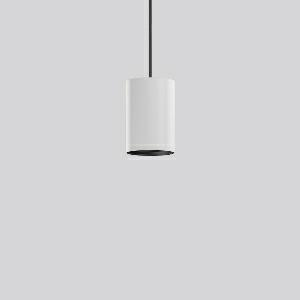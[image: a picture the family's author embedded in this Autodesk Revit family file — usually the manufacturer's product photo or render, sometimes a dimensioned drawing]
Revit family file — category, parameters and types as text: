
# Revit family: deecos_p_maxi_911538_002_3_a3c1
name_source: partatom
category: Lighting Fixtures
units: mm (PartAtom-declared; Revit-internal decimal feet)

## family parameters
Cut with Voids When Loaded = No
Host = Face
Light Source = No
Part Type = Normal
Room Calculation Point = No
Round Connector Dimension = Use Diameter
Shared = No

## types (1)
- DEECOS P maxi (1 x LED Modul 935, 4400 lm, 3500)
    Apparent Load = 35 VA
    Approval mark = CE
    CIE Flux Codes = 100 100 100 100 100
    Color Rendering = 92
    Color Temperature = 3500
    Default Elevation = 1800 mm
    Description = Series: DEECOS P maxi
Cylindrical pendant luminaire. Housing: die-cast aluminium, powder-coated. Canopy made of powder-coated sheet steel with magnetic attachment. Optical assembly with reflector made of MIRO-Silver with 98% total light reflection for outstanding efficiency - can be changed without tools. Best colour rendering index Ra>90. Transparent suspension cable 2 m, can be shortened. High quality converter without flickering and stroboscopic effect. The following accessories can be mounted without use of tools: interchangeable lenses, honeycomb louvre, clear and frosted diffusers, white interchangeable plastic ring. Decorative recessed suspension set available as accessory. 
Colour: traffic white, matt (RAL 9016)
Diameter: 123 mm
Height: 181 mm
Suspension length: 2000 mm
Lamp: LED
Socket: without socket
Colour temperature: 3500K
Colour rendering index (CRI): 92
System power: 35 W
Rated luminous flux: 4400 lm
Luminous efficiency: 126 lm/W
Control gear: Regulated power supply
Protection class: I
Type of protection: IP 20
    Height = 181 mm
    Lamp = 1 x LED Modul 935
    Lamp Light Flux = 4400 lm
    Lamp count = 1
    Length = 123 mm
    Lifetime = 50000 h
    Luminous efficacy = 126 lm/W
    Manufacturer = RZB
    ModVariant = No
    Model = 911538.002.3
    Mounting Place = Ceiling
    Mounting Type = Pendant
    Number of Poles = 1
    OnlyDefault = Yes
    Power Factor = 1
    Product Name = DEECOS P maxi
    Product group = Pendant luminaires
    ProductGroupID = 902
    Protection Class = Protection class I
    Protection Degree = IP 20
    RLX_Detail_Level = 1
    RLX_Emergency_Light_Flux = 0 lm
    RLX_Emergency_Type = 0
    RLX_Emergency_Type_DB = No
    RlxData = <blob elided: 35273 chars, md5=5a482e31>
    Socket = socket
    Standby Power = 0 W
    System Light Flux = 4400 lm
    System Power = 35 W
    Type Comments = Product without accessories
    Type Image = 911480.002.jpg
    URL = http://relux.com
    VarID = ---
    Voltage = 230 V
    Voltage Range = 220-240 V
    Weight = 0.00 kg
    Width = 0 mm  [stored 0 ft]

note: [stored X ft] marks values corroborated as IEEE doubles in the binary element streams (Revit-internal decimal feet)

## geometry (parser evidence)
native form markers: Blend x4, Sweep x9
no freeform markers — native parametric forms only
